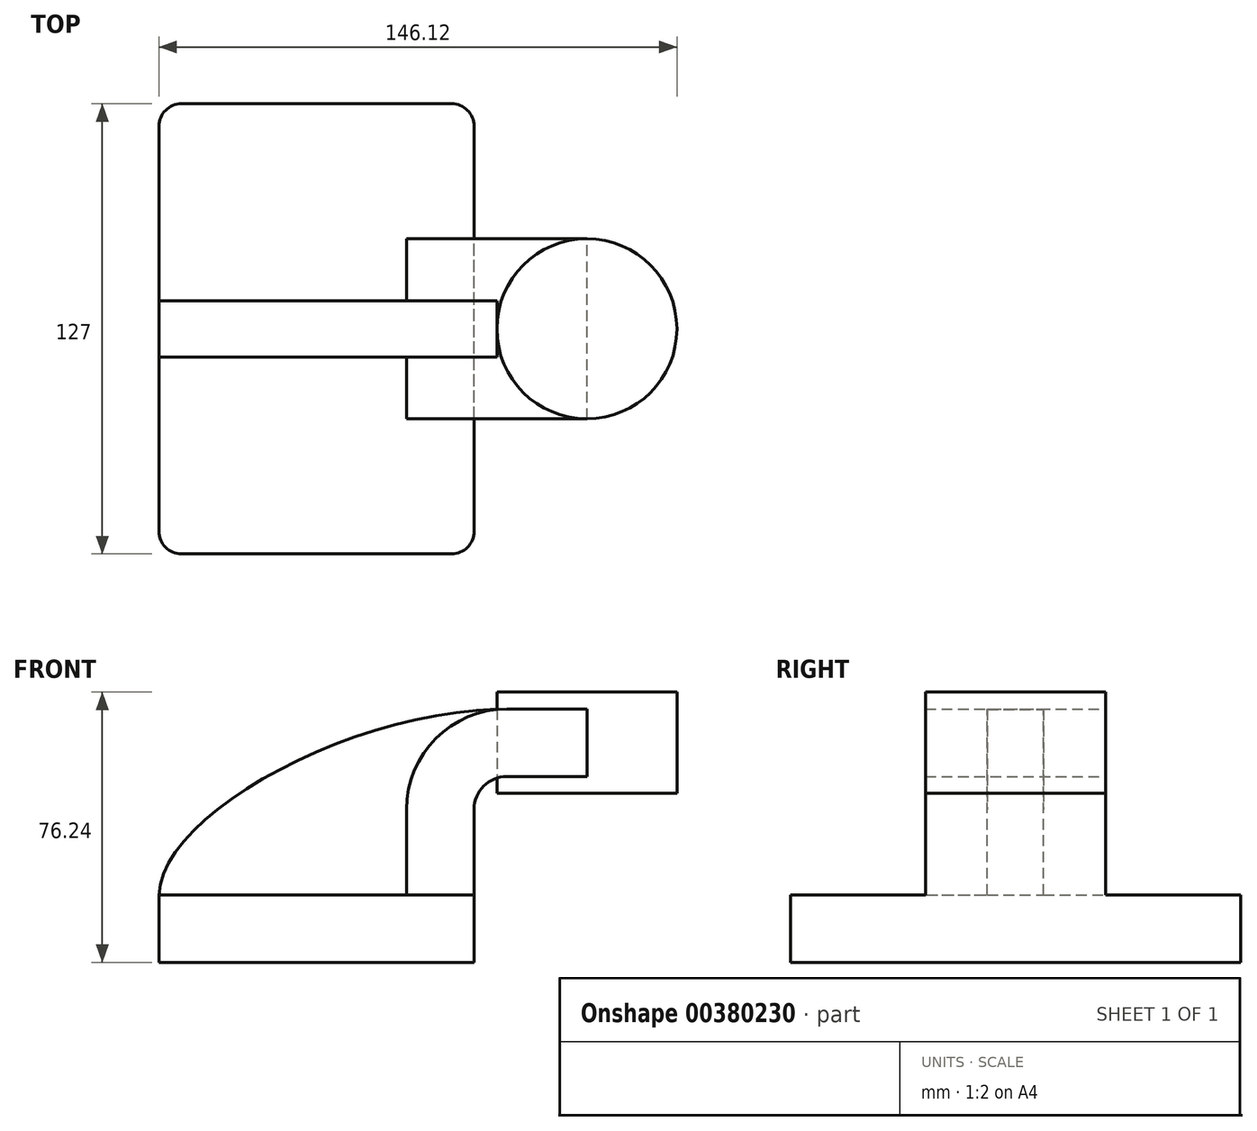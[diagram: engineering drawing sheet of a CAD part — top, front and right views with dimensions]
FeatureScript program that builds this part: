
annotation { "Feature Type Name" : "Feature", "Feature Type Description" : "" }
export const myFeature = defineFeature(function(context is Context, id is Id, definition is map)
    precondition{}
    {
        {
            var Q0;
            Q0=qCreatedBy(makeId("Front.planeOp"),FACE);
            var sketch = newSketch(context, id + "F0", { "sketchPlane" : qUnion([Q0])});
            skLineSegment(sketch, "E0.bottom", {"start": v(-44.45, 9.52) * mm, "end": v(44.45, 9.53) * mm});
            skLineSegment(sketch, "E0.top", {"start": v(-44.45, -9.53) * mm, "end": v(44.45, -9.53) * mm});
            skLineSegment(sketch, "E0.left", {"start": v(-44.45, 9.52) * mm, "end": v(-44.45, -9.53) * mm});
            skLineSegment(sketch, "E0.right", {"start": v(44.45, 9.53) * mm, "end": v(44.45, -9.52) * mm});
            skPoint(sketch, "E0.middle", {"position": v(0, 0) * mm});
            skLineSegment(sketch, "E1.bottom", {"start": v(50.87, 66.71) * mm, "end": v(101.67, 66.71) * mm});
            skLineSegment(sketch, "E1.top", {"start": v(50.87, 38.14) * mm, "end": v(101.67, 38.14) * mm});
            skLineSegment(sketch, "E1.left", {"start": v(50.87, 66.71) * mm, "end": v(50.87, 38.14) * mm});
            skLineSegment(sketch, "E1.right", {"start": v(101.67, 66.71) * mm, "end": v(101.67, 38.14) * mm});
            skPoint(sketch, "E1.middle", {"position": v(76.27, 52.43) * mm});
            skLineSegment(sketch, "E2", {"start": v(44.45, 9.53) * mm, "end": v(44.45, 33.64) * mm});
            skArc(sketch, "E3", {"start": v(44.45, 33.64) * mm, "mid": v(47.16, 40.17) * mm, "end": v(53.69, 42.88) * mm});
            skLineSegment(sketch, "E4", {"start": v(53.69, 42.88) * mm, "end": v(76.27, 42.88) * mm});
            skLineSegment(sketch, "E5.0", {"start": v(53.69, 61.93) * mm, "end": v(76.27, 61.93) * mm});
            skArc(sketch, "E5.1", {"start": v(25.4, 33.64) * mm, "mid": v(33.68, 53.64) * mm, "end": v(53.69, 61.93) * mm});
            skLineSegment(sketch, "E5.2", {"start": v(25.4, 9.53) * mm, "end": v(25.4, 33.64) * mm});
            skLineSegment(sketch, "E6", {"start": v(76.27, 38.14) * mm, "end": v(76.27, 66.71) * mm});
            skFitSpline(sketch, "E7", {"points": [v(-44.45, 9.52) * mm, v(53.69, 61.93) * mm], "startDerivative": vector(1.81, 67.74) * mm, "endDerivative": vector(131.97, 0.1) * mm});
            skSolve(sketch);
        }
        {
            var Q0;
            Q0=makeQuery(id+"F0.imprint","IMPRINT",FACE,{"disambiguationData":[TD([[makeQuery(id+"F0.imprint","IMPRINT",EDGE,{"derivedFrom":sQuery(id+"F0.wireOp",EDGE,"E0.top")}),1.0]])]});
            extrude(context, id + "F1", {"entities" : qUnion([Q0]), "endBound" : BoundingType.SYMMETRIC, "depth" : 127 * mm});
        }
        {
            var Q0;
            {var subQ1=sQuery(id+"F0.wireOp",EDGE,"E2");Q0=makeQuery(id+"F0.imprint","IMPRINT",FACE,{"disambiguationData":[TD([[makeQuery(id+"F0.imprint","IMPRINT",EDGE,{"derivedFrom":subQ1}),1.0]])]});}
            var Q1;
            {var subQ1=sQuery(id+"F0.wireOp",EDGE,"E4");Q1=makeQuery(id+"F0.imprint","IMPRINT",FACE,{"disambiguationData":[TD([[makeQuery(id+"F0.imprint","IMPRINT",EDGE,{"derivedFrom":subQ1}),1.0]])]});}
            extrude(context, id + "F2", {"entities" : qUnion([Q0, Q1]), "operationType" : NewBodyOperationType.ADD, "endBound" : BoundingType.SYMMETRIC, "depth" : 50.8 * mm});
        }
        {
            var Q0;
            {var subQ0=sQuery(id+"F0.wireOp",EDGE,"E5.2");Q0=makeQuery(id+"F0.imprint","IMPRINT",FACE,{"disambiguationData":[TD([[makeQuery(id+"F0.imprint","IMPRINT",EDGE,{"derivedFrom":subQ0}),1.0]])]});}
            extrude(context, id + "F3", {"entities" : qUnion([Q0]), "operationType" : NewBodyOperationType.ADD, "endBound" : BoundingType.SYMMETRIC, "depth" : 15.88 * mm});
        }
        {
            var Q0;
            Q0=makeQuery(id+"F1.opExtrude","CAP_EDGE",EDGE,{"disambiguationData":[OSD([sQuery(id+"F0.wireOp",EDGE,"E0.left")])],"isStart":false});
            var Q1;
            Q1=makeQuery(id+"F1.opExtrude","CAP_EDGE",EDGE,{"disambiguationData":[OSD([sQuery(id+"F0.wireOp",EDGE,"E0.right")])],"isStart":false});
            var Q2;
            Q2=makeQuery(id+"F1.opExtrude","CAP_EDGE",EDGE,{"disambiguationData":[OSD([sQuery(id+"F0.wireOp",EDGE,"E0.right")])],"isStart":true});
            var Q3;
            Q3=makeQuery(id+"F1.opExtrude","CAP_EDGE",EDGE,{"disambiguationData":[OSD([sQuery(id+"F0.wireOp",EDGE,"E0.left")])],"isStart":true});
            fillet(context, id + "F4", {"entities" : qUnion([Q0, Q1, Q2, Q3]), "radius" : 6.35 * mm, "tangentPropagation" : true, "allowEdgeOverflow" : false});
        }
        {
            var Q0;
            {var subQ4=sQuery(id+"F0.wireOp",EDGE,"E1.right");Q0=makeQuery(id+"F0.imprint","IMPRINT",FACE,{"disambiguationData":[TD([[makeQuery(id+"F0.imprint","IMPRINT",EDGE,{"derivedFrom":subQ4}),-1.0]])]});}
            var Q1;
            Q1=sQuery(id+"F0.wireOp",EDGE,"E6");
            var Q2;
            Q2=sQuery(id+"F0.wireOp",EDGE,"E1.left");
            var Q3;
            Q3=sQuery(id+"F0.wireOp",EDGE,"E6");
            revolve(context, id + "F5", {"entities" : qUnion([Q0]), "surfaceEntities" : qUnion([Q1, Q2]), "axis" : qUnion([Q3]), "revolveType" : RevolveType.FULL});
        }
    });
